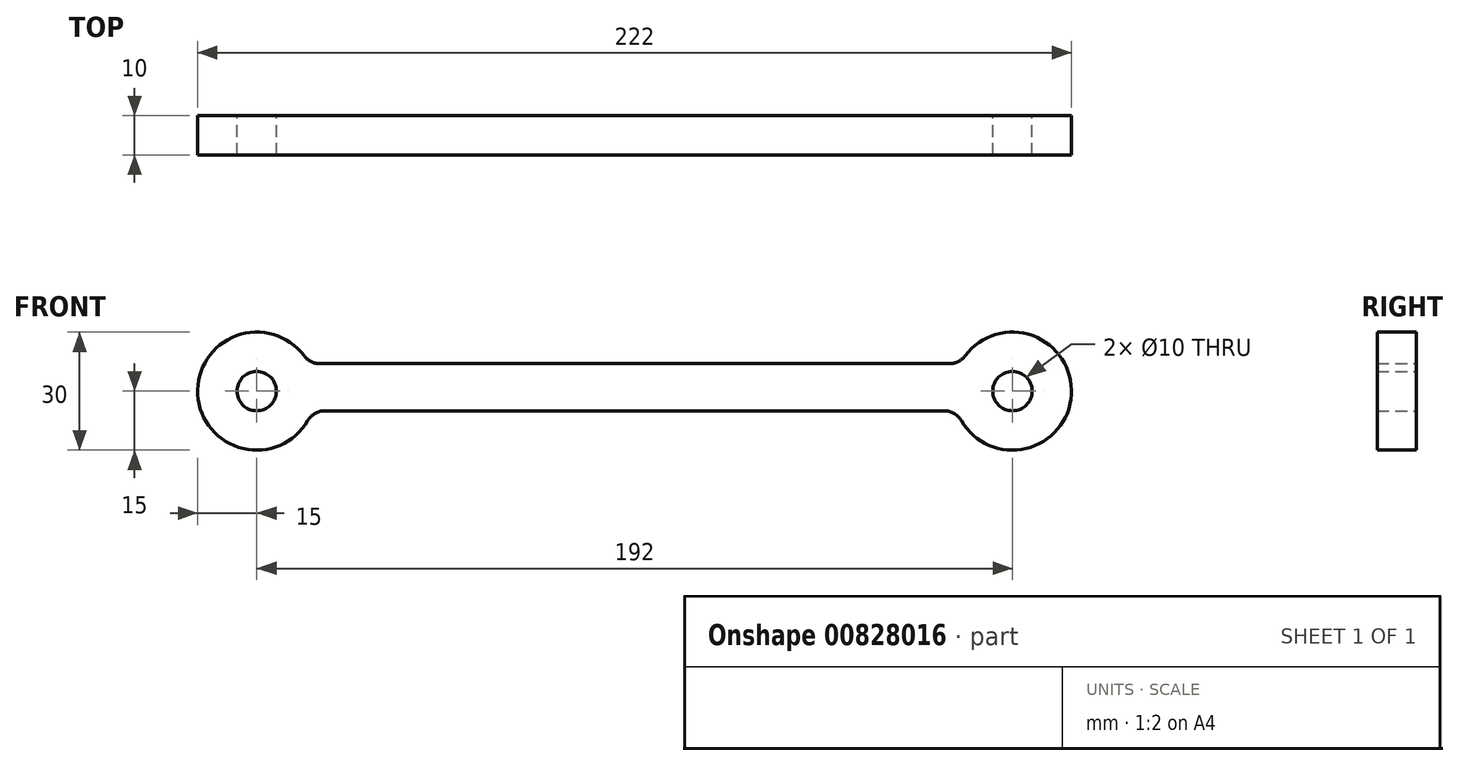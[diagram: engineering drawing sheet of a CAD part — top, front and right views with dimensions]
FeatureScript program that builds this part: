
annotation { "Feature Type Name" : "Feature", "Feature Type Description" : "" }
export const myFeature = defineFeature(function(context is Context, id is Id, definition is map)
    precondition{}
    {
        {
            var Q0;
            Q0=qCreatedBy(makeId("Front.planeOp"),FACE);
            var sketch = newSketch(context, id + "F0", { "sketchPlane" : qUnion([Q0])});
            skLineSegment(sketch, "E0.bottom", {"start": v(-78.68, -7) * mm, "end": v(0, -7) * mm});
            skLineSegment(sketch, "E0.top", {"start": v(-80, 5) * mm, "end": v(0, 5) * mm});
            skPoint(sketch, "E0.middle", {"position": v(0, 0) * mm});
            skArc(sketch, "E1", {"start": v(-84, 7) * mm, "mid": v(-110.97, -2.9) * mm, "end": v(-83, -9.5) * mm});
            skCircle(sketch, "E2", {"center": v(-96, -2) * mm, "radius": 5 * mm});
            skPoint(sketch, "E3.visualSharp", {"position": v(-82.73, 5) * mm});
            skArc(sketch, "E3.filletArc", {"start": v(-84, 7) * mm, "mid": v(-82.24, 5.53) * mm, "end": v(-80, 5) * mm});
            skPoint(sketch, "E4.visualSharp", {"position": v(-81.86, -7) * mm});
            skArc(sketch, "E4.filletArc", {"start": v(-78.68, -7) * mm, "mid": v(-81.18, -7.67) * mm, "end": v(-83, -9.5) * mm});
            skLineSegment(sketch, "E5", {"start": v(0, 14.13) * mm, "end": v(0, -18.04) * mm, "construction": true});
            skArc(sketch, "E6.MirrorCS", {"start": v(78.68, -7) * mm, "mid": v(81.18, -7.67) * mm, "end": v(83, -9.5) * mm});
            skArc(sketch, "E7.MirrorCS", {"start": v(84, 7) * mm, "mid": v(82.24, 5.53) * mm, "end": v(80, 5) * mm});
            skPoint(sketch, "E8.MirrorP", {"position": v(82.73, 5) * mm});
            skCircle(sketch, "E9.MirrorC", {"center": v(96, -2) * mm, "radius": 5 * mm});
            skArc(sketch, "E10.MirrorCS", {"start": v(84, 7) * mm, "mid": v(110.97, -2.9) * mm, "end": v(83, -9.5) * mm});
            skLineSegment(sketch, "E11.MirrorCS", {"start": v(80, 5) * mm, "end": v(0, 5) * mm});
            skPoint(sketch, "E12.MirrorP", {"position": v(81.86, -7) * mm});
            skLineSegment(sketch, "E13.MirrorCS", {"start": v(78.68, -7) * mm, "end": v(0, -7) * mm});
            skSolve(sketch);
        }
        {
            var Q0;
            Q0=makeQuery(id+"F0.imprint","IMPRINT",FACE,{"disambiguationData":[TD([[makeQuery(id+"F0.imprint","IMPRINT",EDGE,{"derivedFrom":sQuery(id+"F0.wireOp",EDGE,"E0.bottom")}),1.0]])]});
            extrude(context, id + "F1", {"entities" : qUnion([Q0]), "depth" : 10 * mm, "offsetDistance" : 25.4 * mm});
        }
    });
